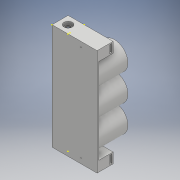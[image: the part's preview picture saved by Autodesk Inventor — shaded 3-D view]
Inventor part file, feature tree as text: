
AUTODESK INVENTOR PART (.ipt)
format: ipt  version: 2018 (Build 220112000, 112)  size: 285,184 bytes
history: native  units: mm
features: sketch x23, extrude x15, fillet x2
ambient origin geometry x8: Origin, YZ Plane, XZ Plane, XY Plane, X Axis, Y Axis, Z Axis, Center Point
bodies: Solid1 (feature_tree)
feature tree (40):
  extrude  "Extrusion1"  Depth=165.0mm
  extrude  "Extrusion2"  Depth=7.0mm
  sketch  "Sketch3"  dims[d5=7.0mm d6=22.0mm d7=0.0mm]
  extrude  "Extrusion3"  Depth=22.0mm TaperAngle=0.0deg
  extrude  "Extrusion4"  Depth=5.0mm TaperAngle=0.0deg
  extrude  "Extrusion5"  Depth=10.0mm
  sketch  "Sketch7"  dims[d18=7.5mm d19=0.0mm d20=2.0mm]
  sketch  "Sketch8"  dims[d21=3.0mm d22=45.0mm d23=0.0mm]
  extrude  "Extrusion6"  Depth=5.0mm
  fillet  "Fillet1"  Radius=5.0mm
  extrude  "Extrusion7"  Depth=2.0mm
  extrude  "Extrusion8"  Depth=45.0mm TaperAngle=0.0deg
  sketch  "Sketch12"  dims[d31=16.0mm d32=22.0mm d33=0.0mm]
  extrude  "Extrusion9"  Depth=38.65mm
  sketch  "Sketch14"  dims[d37=3.25mm d38=3.5mm d39=12.25mm]
  sketch  "Sketch15"  dims[d40=3.25mm d41=40.0mm d42=0.0mm]
  extrude  "Extrusion10"  Depth=38.65mm
  extrude  "Extrusion11"  Depth=16.0mm
  extrude  "Extrusion12"  Depth=22.0mm TaperAngle=0.0deg
  sketch  "Sketch17"  dims[d45=25.0mm]
  sketch  "Sketch18"  dims[d46=1.5mm]
  sketch  "Sketch19"  dims[d47=25.0mm d48=0.0mm]
  extrude  "Extrusion13"  Depth=12.25mm
  sketch  "Sketch21"  dims[d50=1.5mm]
  extrude  "Extrusion14"  Depth=3.5mm
  fillet  "Fillet2"  Radius=12.25mm
  extrude  "Extrusion15"  Depth=40.0mm TaperAngle=0.0deg
  sketch  "Sketch1"  dims[d0=25.0mm d1=165.0mm]
  sketch  "Sketch2"  dims[d2=3.0mm d3=0.0mm d4=7.0mm]
  sketch  "Sketch4"  dims[d8=13.0mm d9=5.0mm d10=0.0mm]
  sketch  "Sketch5"  dims[d11=5.0mm d12=0.0mm d13=10.0mm]
  sketch  "Sketch6"  dims[d14=165.0mm d15=0.0mm d16=5.0mm d17=5.0mm]
  sketch  "Sketch9"  dims[d24=42.0mm d25=38.65mm]
  sketch  "Sketch10"  dims[d26=38.65mm d27=38.65mm]
  sketch  "Sketch11"  dims[d28=45.0mm d29=0.0mm d30=16.0mm]
  sketch  "Sketch13"  dims[d35=3.5mm d36=12.25mm]
  sketch  "Sketch16"  dims[d43=40.0mm d44=0.0mm]
  sketch  "Sketch20"  dims[d49=25.0mm]
  sketch  "Sketch22"  dims[d51=25.0mm d52=0.0mm]
  sketch  "Sketch23"  dims[d53=2.0mm d54=1.0mm d55=5.25mm d56=0.0mm d57=1.0mm d58=1.0mm d59=5.25mm d60=0.0mm]
